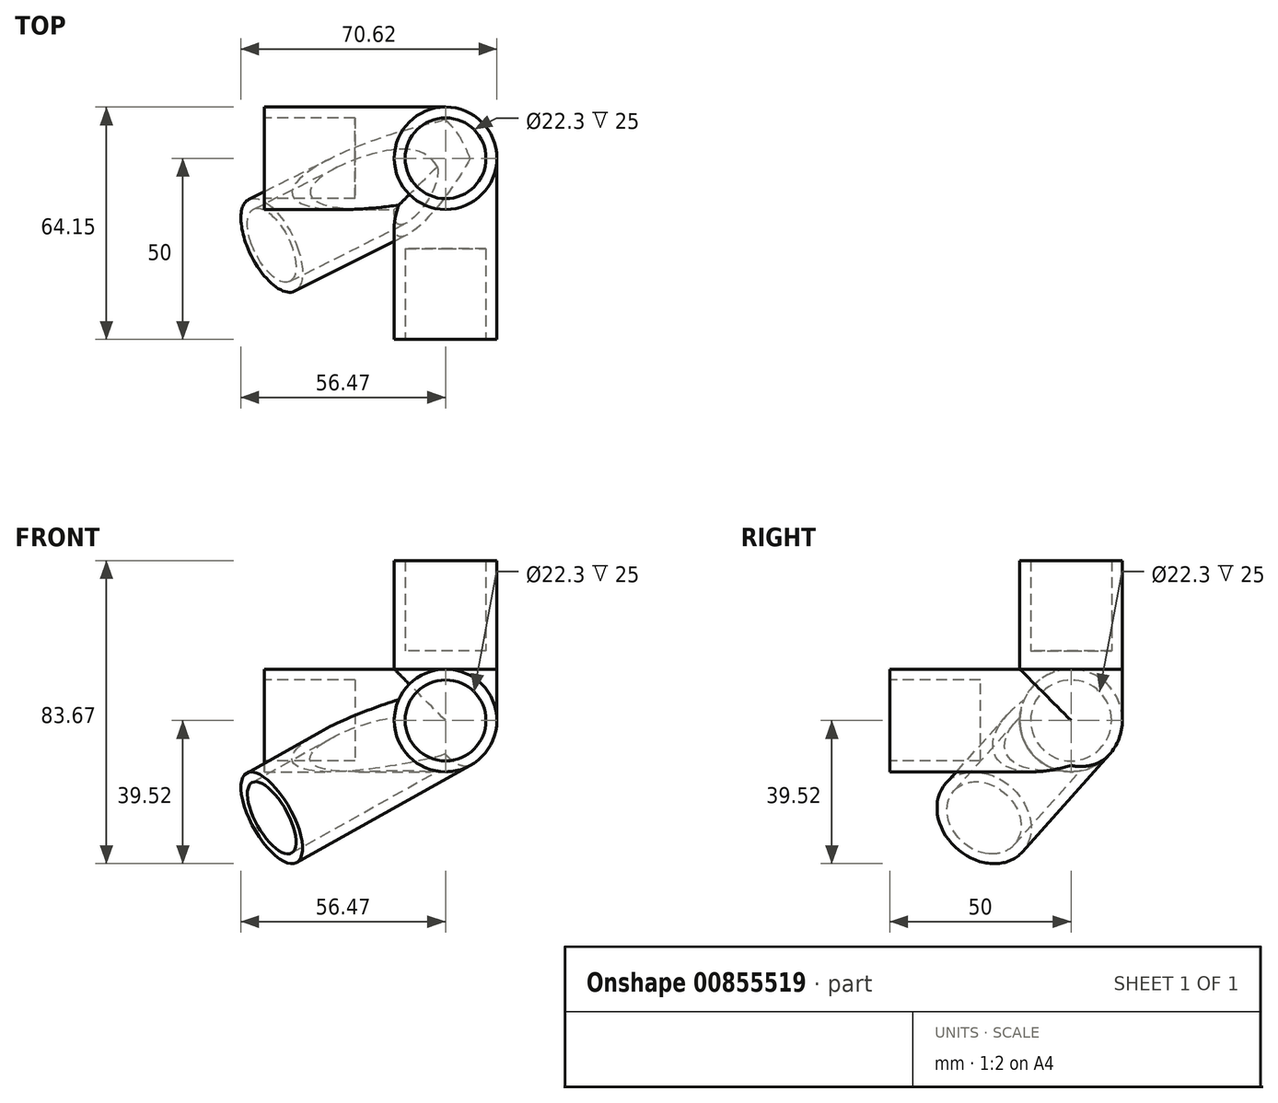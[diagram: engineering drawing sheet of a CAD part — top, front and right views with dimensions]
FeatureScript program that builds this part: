
annotation { "Feature Type Name" : "Feature", "Feature Type Description" : "" }
export const myFeature = defineFeature(function(context is Context, id is Id, definition is map)
    precondition{}
    {
        {
            var Q0;
            Q0=qCreatedBy(makeId("Top.planeOp"),FACE);
            var sketch = newSketch(context, id + "F0", { "sketchPlane" : qUnion([Q0])});
            skCircle(sketch, "E0", {"center": v(0, 0) * mm, "radius": 11.15 * mm});
            skCircle(sketch, "E1", {"center": v(0, 0) * mm, "radius": 14.15 * mm});
            skSolve(sketch);
        }
        {
            var Q0;
            Q0 = qSketchRegion(id + "F0", true);
            extrude(context, id + "F1", {"entities" : qUnion([Q0]), "depth" : 25 * mm, "offsetDistance" : 25 * mm});
        }
        {
            var Q0;
            Q0=qCreatedBy(makeId("Top.planeOp"),FACE);
            var sketch = newSketch(context, id + "F2", { "sketchPlane" : qUnion([Q0])});
            skCircle(sketch, "E2", {"center": v(0, 0) * mm, "radius": 14.15 * mm});
            skSolve(sketch);
        }
        {
            var Q0;
            Q0 = qSketchRegion(id + "F2", true);
            extrude(context, id + "F3", {"entities" : qUnion([Q0]), "operationType" : NewBodyOperationType.ADD, "oppositeDirection" : true, "depth" : 5 * mm, "offsetDistance" : 25 * mm});
        }
        {
            var Q0;
            Q0=qCreatedBy(makeId("Right.planeOp"),FACE);
            var sketch = newSketch(context, id + "F4", { "sketchPlane" : qUnion([Q0])});
            skLineSegment(sketch, "E3", {"start": v(0, 0) * mm, "end": v(0, -5) * mm, "construction": true});
            skLineSegment(sketch, "E4", {"start": v(0, -5) * mm, "end": v(0, -19.15) * mm, "construction": true});
            skCircle(sketch, "E5", {"center": v(0, -19.15) * mm, "radius": 14.15 * mm});
            skCircle(sketch, "E6", {"center": v(0, -19.15) * mm, "radius": 11.15 * mm});
            skSolve(sketch);
        }
        {
            var Q0;
            Q0 = qSketchRegion(id + "F4", true);
            extrude(context, id + "F5", {"entities" : qUnion([Q0]), "operationType" : NewBodyOperationType.ADD, "oppositeDirection" : true, "depth" : 50 * mm, "offsetDistance" : 25 * mm});
        }
        {
            var Q0;
            Q0=qCreatedBy(makeId("Front.planeOp"),FACE);
            var sketch = newSketch(context, id + "F6", { "sketchPlane" : qUnion([Q0])});
            skLineSegment(sketch, "E7", {"start": v(0, 0) * mm, "end": v(0, -5) * mm, "construction": true});
            skLineSegment(sketch, "E8", {"start": v(0, -5) * mm, "end": v(0, -19.15) * mm, "construction": true});
            skCircle(sketch, "E9", {"center": v(0, -19.15) * mm, "radius": 14.15 * mm});
            skCircle(sketch, "E10", {"center": v(0, -19.15) * mm, "radius": 11.15 * mm});
            skSolve(sketch);
        }
        {
            var Q0;
            Q0 = qSketchRegion(id + "F6", true);
            extrude(context, id + "F7", {"entities" : qUnion([Q0]), "operationType" : NewBodyOperationType.ADD, "depth" : 50 * mm, "offsetDistance" : 25 * mm});
        }
        {
            var Q0;
            {var subQ0=sQuery(id+"F4.wireOp",EDGE,"E6");var subQ1=sQuery(id+"F4.wireOp",EDGE,"E5");var subQ2=sQuery(id+"F6.wireOp",EDGE,"E10");var subQ3=sQuery(id+"F6.wireOp",EDGE,"E9");var subQ4=makeQuery(id+"F7.opExtrude","CAP_FACE",FACE,{"disambiguationData":[OSD([subQ3,subQ2])],"isStart":true});Q0=makeQuery(id+"F7.boolean.opBoolean","SPLIT",FACE,{"disambiguationData":[TD([makeQuery(id+"F5.opExtrude","SWEPT_FACE",FACE,{"disambiguationData":[OSD([subQ1])]}),makeQuery(id+"F5.opExtrude","CAP_FACE",FACE,{"disambiguationData":[OSD([subQ1,subQ0])],"isStart":true}),makeQuery(id+"F5.opExtrude","SWEPT_FACE",FACE,{"disambiguationData":[OSD([subQ0])]}),makeQuery(id+"F7.opExtrude","SWEPT_FACE",FACE,{"disambiguationData":[OSD([subQ3])]}),subQ4,makeQuery(id+"F7.opExtrude","SWEPT_FACE",FACE,{"disambiguationData":[OSD([subQ2])]})])],"derivedFrom":subQ4});}
            var sketch = newSketch(context, id + "F8", { "sketchPlane" : qUnion([Q0])});
            skArc(sketch, "E11", {"start": v(-14.15, -19.15) * mm, "mid": v(-10, -29.16) * mm, "end": v(0, -33.3) * mm});
            skLineSegment(sketch, "E12", {"start": v(0, -5) * mm, "end": v(-14.15, -5) * mm});
            skLineSegment(sketch, "E13", {"start": v(-14.15, -19.15) * mm, "end": v(-14.15, -5) * mm});
            skLineSegment(sketch, "E14", {"start": v(0, -33.3) * mm, "end": v(0, -5) * mm});
            skSolve(sketch);
        }
        {
            var Q0;
            Q0 = qSketchRegion(id + "F8", true);
            var Q1;
            Q1=sQuery(id+"F8.wireOp",EDGE,"E14");
            revolve(context, id + "F9", {"surfaceOperationType" : NewSurfaceOperationType.NEW, "entities" : qUnion([Q0]), "axis" : qUnion([Q1]), "revolveType" : RevolveType.ONE_DIRECTION, "angle" : 360 * degree});
        }
        {
            var Q0;
            Q0=makeQuery(id+"F5.opExtrude","CAP_FACE",FACE,{"disambiguationData":[OSD([sQuery(id+"F4.wireOp",EDGE,"E5"),sQuery(id+"F4.wireOp",EDGE,"E6")])],"isStart":false});
            var sketch = newSketch(context, id + "F10", { "sketchPlane" : qUnion([Q0])});
            skLineSegment(sketch, "E15", {"start": v(0, 0) * mm, "end": v(0, -33.3) * mm, "construction": true});
            skPoint(sketch, "E16.center.orphan", {"position": v(0, -19.15) * mm});
            skCircle(sketch, "E17", {"center": v(0, -19.15) * mm, "radius": 11.15 * mm});
            skSolve(sketch);
        }
        {
            var Q0;
            Q0=makeQuery(id+"F7.opExtrude","CAP_FACE",FACE,{"disambiguationData":[OSD([sQuery(id+"F6.wireOp",EDGE,"E9"),sQuery(id+"F6.wireOp",EDGE,"E10")])],"isStart":false});
            var sketch = newSketch(context, id + "F11", { "sketchPlane" : qUnion([Q0])});
            skCircle(sketch, "E18", {"center": v(0, -19.15) * mm, "radius": 11.15 * mm});
            skSolve(sketch);
        }
        {
            var Q0;
            Q0=qCreatedBy(makeId("Right.planeOp"),FACE);
            var sketch = newSketch(context, id + "F12", { "sketchPlane" : qUnion([Q0])});
            skLineSegment(sketch, "E19", {"start": v(0, 43.35) * mm, "end": v(0, -51.42) * mm, "construction": true});
            skSolve(sketch);
        }
        {
            var Q0;
            Q0=sQuery(id+"F12.wireOp",EDGE,"E19");
            var Q1;
            Q1=qCreatedBy(makeId("Front.planeOp"),FACE);
            cPlane(context, id + "F13", {"entities" : qUnion([Q0, Q1]), "cplaneType" : CPlaneType.LINE_ANGLE, "offset" : 25 * mm, "angle" : 26.6 * degree, "oppositeDirection" : true, "width" : 150 * mm, "height" : 150 * mm});
        }
        {
            var Q0;
            Q0=qCreatedBy(id+"F13.planeOp",FACE);
            var sketch = newSketch(context, id + "F14", { "sketchPlane" : qUnion([Q0])});
            skLineSegment(sketch, "E20", {"start": v(0, 0) * mm, "end": v(0, -19.15) * mm, "construction": true});
            skLineSegment(sketch, "E21", {"start": v(0, -33.3) * mm, "end": v(0, -19.15) * mm, "construction": true});
            skLineSegment(sketch, "E22", {"start": v(0, -19.15) * mm, "end": v(26.82, -32.58) * mm, "construction": true});
            skLineSegment(sketch, "E23", {"start": v(0, -19.15) * mm, "end": v(69.41, -19.15) * mm, "construction": true});
            skSolve(sketch);
        }
        {
            var Q0;
            Q0=sQuery(id+"F14.wireOp",VERTEX,"E22.end");
            var Q1;
            Q1=sQuery(id+"F14.wireOp",EDGE,"E22");
            cPlane(context, id + "F15", {"entities" : qUnion([Q0, Q1]), "cplaneType" : CPlaneType.LINE_POINT, "offset" : 25 * mm, "width" : 150 * mm, "height" : 150 * mm});
        }
        {
            var Q0;
            Q0=qCreatedBy(id+"F15.planeOp",FACE);
            var sketch = newSketch(context, id + "F16", { "sketchPlane" : qUnion([Q0])});
            skCircle(sketch, "E24", {"center": v(-3.75, -16.7) * mm, "radius": 14.15 * mm});
            skCircle(sketch, "E25", {"center": v(-3.75, -16.7) * mm, "radius": 11.15 * mm});
            skSolve(sketch);
        }
        {
            var Q0;
            Q0 = qSketchRegion(id + "F16", true);
            extrude(context, id + "F17", {"entities" : qUnion([Q0]), "operationType" : NewBodyOperationType.ADD, "endBound" : BoundingType.SYMMETRIC, "depth" : 60 * mm, "offsetDistance" : 25 * mm});
        }
        {
            var Q0;
            Q0 = qSketchRegion(id + "F10", true);
            extrude(context, id + "F18", {"entities" : qUnion([Q0]), "operationType" : NewBodyOperationType.REMOVE, "oppositeDirection" : true, "depth" : 35 * mm, "offsetDistance" : 25 * mm});
        }
        {
            var Q0;
            Q0 = qSketchRegion(id + "F11", true);
            extrude(context, id + "F19", {"entities" : qUnion([Q0]), "operationType" : NewBodyOperationType.REMOVE, "oppositeDirection" : true, "depth" : 30 * mm, "offsetDistance" : 25 * mm});
        }
        {
            var Q0;
            Q0=makeQuery(id+"F5.opExtrude","CAP_FACE",FACE,{"disambiguationData":[OSD([sQuery(id+"F4.wireOp",EDGE,"E5"),sQuery(id+"F4.wireOp",EDGE,"E6")])],"isStart":false});
            var sketch = newSketch(context, id + "F20", { "sketchPlane" : qUnion([Q0])});
            skCircle(sketch, "E26", {"center": v(0, -19.15) * mm, "radius": 11.15 * mm});
            skSolve(sketch);
        }
        {
            var Q0;
            Q0 = qSketchRegion(id + "F20", true);
            extrude(context, id + "F21", {"entities" : qUnion([Q0]), "operationType" : NewBodyOperationType.ADD, "oppositeDirection" : true, "depth" : 50 * mm, "offsetDistance" : 25 * mm});
        }
        {
            var Q0;
            Q0=makeQuery(id+"F21.boolean.opBoolean","MERGE",FACE,{"derivedFrom":[makeQuery(id+"F5.opExtrude","CAP_FACE",FACE,{"disambiguationData":[OSD([sQuery(id+"F4.wireOp",EDGE,"E5"),sQuery(id+"F4.wireOp",EDGE,"E6")])],"isStart":false}),makeQuery(id+"F21.opExtrude","CAP_FACE",FACE,{"disambiguationData":[OSD([sQuery(id+"F20.wireOp",EDGE,"E26")])],"isStart":true})]});
            var sketch = newSketch(context, id + "F22", { "sketchPlane" : qUnion([Q0])});
            skCircle(sketch, "E27", {"center": v(0, -19.15) * mm, "radius": 11.15 * mm});
            skSolve(sketch);
        }
        {
            var Q0;
            Q0 = qSketchRegion(id + "F22", true);
            extrude(context, id + "F23", {"entities" : qUnion([Q0]), "operationType" : NewBodyOperationType.REMOVE, "oppositeDirection" : true, "depth" : 25 * mm, "offsetDistance" : 25 * mm});
        }
        {
            var Q0;
            Q0=makeQuery(id+"F7.opExtrude","CAP_FACE",FACE,{"disambiguationData":[OSD([sQuery(id+"F6.wireOp",EDGE,"E9"),sQuery(id+"F6.wireOp",EDGE,"E10")])],"isStart":false});
            var sketch = newSketch(context, id + "F24", { "sketchPlane" : qUnion([Q0])});
            skCircle(sketch, "E28", {"center": v(0, -19.15) * mm, "radius": 11.15 * mm});
            skSolve(sketch);
        }
        {
            var Q0;
            Q0 = qSketchRegion(id + "F24", true);
            extrude(context, id + "F25", {"entities" : qUnion([Q0]), "operationType" : NewBodyOperationType.ADD, "oppositeDirection" : true, "depth" : 50.1 * mm, "offsetDistance" : 25 * mm});
        }
        {
            var Q0;
            Q0=makeQuery(id+"F25.boolean.opBoolean","MERGE",FACE,{"derivedFrom":[makeQuery(id+"F7.opExtrude","CAP_FACE",FACE,{"disambiguationData":[OSD([sQuery(id+"F6.wireOp",EDGE,"E9"),sQuery(id+"F6.wireOp",EDGE,"E10")])],"isStart":false}),makeQuery(id+"F25.opExtrude","CAP_FACE",FACE,{"disambiguationData":[OSD([sQuery(id+"F24.wireOp",EDGE,"E28")])],"isStart":true})]});
            var sketch = newSketch(context, id + "F26", { "sketchPlane" : qUnion([Q0])});
            skCircle(sketch, "E29", {"center": v(0, -19.15) * mm, "radius": 11.15 * mm});
            skSolve(sketch);
        }
        {
            var Q0;
            Q0 = qSketchRegion(id + "F26", true);
            extrude(context, id + "F27", {"entities" : qUnion([Q0]), "operationType" : NewBodyOperationType.REMOVE, "oppositeDirection" : true, "depth" : 25 * mm, "offsetDistance" : 25 * mm});
        }
    });
